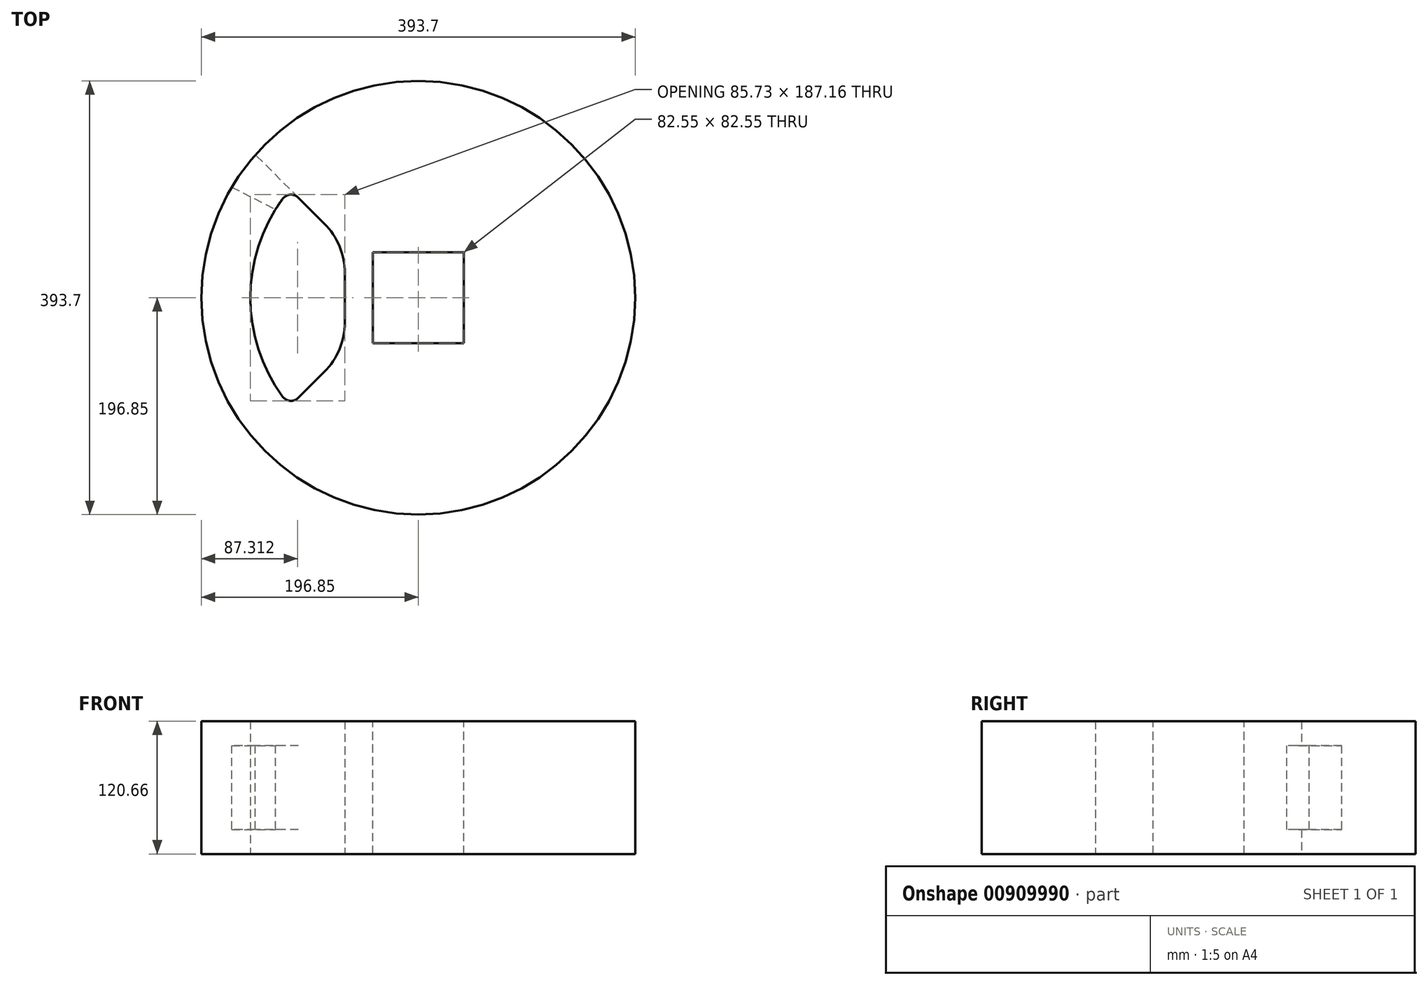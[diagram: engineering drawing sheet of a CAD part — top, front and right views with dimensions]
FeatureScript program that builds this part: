
annotation { "Feature Type Name" : "Feature", "Feature Type Description" : "" }
export const myFeature = defineFeature(function(context is Context, id is Id, definition is map)
    precondition{}
    {
        {
            var Q0;
            Q0=qCreatedBy(makeId("Front.planeOp"),FACE);
            var sketch = newSketch(context, id + "F0", { "sketchPlane" : qUnion([Q0])});
            skLineSegment(sketch, "E0.bottom", {"start": v(0, -60.33) * mm, "end": v(196.85, -60.33) * mm});
            skLineSegment(sketch, "E0.top", {"start": v(0, 60.33) * mm, "end": v(196.85, 60.33) * mm});
            skLineSegment(sketch, "E0.left", {"start": v(0, -60.33) * mm, "end": v(0, 60.32) * mm});
            skLineSegment(sketch, "E0.right", {"start": v(196.85, -60.33) * mm, "end": v(196.85, 60.33) * mm});
            skLineSegment(sketch, "E1", {"start": v(196.85, 0) * mm, "end": v(0, 0) * mm, "construction": true});
            skLineSegment(sketch, "E2", {"start": v(0, 60.33) * mm, "end": v(0, 111.18) * mm, "construction": true});
            skSolve(sketch);
        }
        {
            var Q0;
            Q0=makeQuery(id+"F0.imprint","IMPRINT",FACE,{"disambiguationData":[TD([[makeQuery(id+"F0.imprint","IMPRINT",EDGE,{"derivedFrom":sQuery(id+"F0.wireOp",EDGE,"E0.bottom")}),1.0]])]});
            var Q1;
            Q1=sQuery(id+"F0.wireOp",EDGE,"E0.left");
            revolve(context, id + "F1", {"surfaceOperationType" : NewSurfaceOperationType.NEW, "entities" : qUnion([Q0]), "axis" : qUnion([Q1]), "revolveType" : RevolveType.FULL});
        }
        {
            var Q0;
            Q0=qCreatedBy(makeId("Top.planeOp"),FACE);
            var sketch = newSketch(context, id + "F2", { "sketchPlane" : qUnion([Q0])});
            skArc(sketch, "E3", {"start": v(-116.37, 98.4) * mm, "mid": v(-152.4, 0) * mm, "end": v(-116.37, -98.4) * mm});
            skLineSegment(sketch, "E4.left", {"start": v(-66.67, 22.41) * mm, "end": v(-66.67, -22.41) * mm});
            skLineSegment(sketch, "E5", {"start": v(-116.37, -98.4) * mm, "end": v(-85.27, -67.31) * mm});
            skLineSegment(sketch, "E6", {"start": v(-116.37, 98.4) * mm, "end": v(-85.27, 67.31) * mm});
            skLineSegment(sketch, "E7.bottom", {"start": v(-41.28, 41.28) * mm, "end": v(41.28, 41.28) * mm});
            skLineSegment(sketch, "E7.top", {"start": v(-41.27, -41.28) * mm, "end": v(41.28, -41.28) * mm});
            skLineSegment(sketch, "E7.left", {"start": v(-41.28, 41.28) * mm, "end": v(-41.28, -41.28) * mm});
            skLineSegment(sketch, "E7.right", {"start": v(41.28, 41.28) * mm, "end": v(41.27, -41.28) * mm});
            skLineSegment(sketch, "E8", {"start": v(0, 41.28) * mm, "end": v(0, -41.28) * mm, "construction": true});
            skLineSegment(sketch, "E9", {"start": v(41.28, 0) * mm, "end": v(-41.28, 0) * mm, "construction": true});
            skPoint(sketch, "E10.visualSharp", {"position": v(-66.68, 48.71) * mm});
            skArc(sketch, "E10.filletArc", {"start": v(-66.67, 22.41) * mm, "mid": v(-71.5, 46.71) * mm, "end": v(-85.27, 67.31) * mm});
            skPoint(sketch, "E11.visualSharp", {"position": v(-66.67, -48.71) * mm});
            skArc(sketch, "E11.filletArc", {"start": v(-85.27, -67.31) * mm, "mid": v(-71.5, -46.71) * mm, "end": v(-66.67, -22.41) * mm});
            skLineSegment(sketch, "E12", {"start": v(-116.37, 98.4) * mm, "end": v(-147.88, 129.92) * mm});
            skLineSegment(sketch, "E13", {"start": v(-169.26, 100.5) * mm, "end": v(-129.55, 80.26) * mm});
            skArc(sketch, "E14", {"start": v(-147.88, 129.92) * mm, "mid": v(-159.25, 115.7) * mm, "end": v(-169.26, 100.5) * mm});
            skSolve(sketch);
        }
        {
            var Q0;
            Q0=makeQuery(id+"F2.imprint","IMPRINT",FACE,{"disambiguationData":[TD([[makeQuery(id+"F2.imprint","IMPRINT",EDGE,{"derivedFrom":sQuery(id+"F2.wireOp",EDGE,"E3")}),1.0]])]});
            extrude(context, id + "F3", {"entities" : qUnion([Q0]), "operationType" : NewBodyOperationType.REMOVE, "depth" : 254 * mm, "offsetDistance" : 25 * mm, "symmetric" : true});
        }
        {
            var Q0;
            Q0=makeQuery(id+"F2.imprint","IMPRINT",FACE,{"disambiguationData":[TD([[makeQuery(id+"F2.imprint","IMPRINT",EDGE,{"derivedFrom":sQuery(id+"F2.wireOp",EDGE,"E7.bottom")}),-1.0]])]});
            extrude(context, id + "F4", {"entities" : qUnion([Q0]), "operationType" : NewBodyOperationType.REMOVE, "oppositeDirection" : true, "depth" : 254 * mm, "offsetDistance" : 25 * mm, "symmetric" : true});
        }
        {
            var Q0;
            {var subQ3=sQuery(id+"F2.wireOp",EDGE,"E13");Q0=makeQuery(id+"F2.imprint","IMPRINT",FACE,{"disambiguationData":[TD([[makeQuery(id+"F2.imprint","IMPRINT",EDGE,{"derivedFrom":subQ3}),1.0]])]});}
            extrude(context, id + "F5", {"entities" : qUnion([Q0]), "operationType" : NewBodyOperationType.REMOVE, "oppositeDirection" : true, "depth" : 76.2 * mm, "offsetDistance" : 25 * mm, "symmetric" : true});
        }
        {
            var Q0;
            {var subQ0=sQuery(id+"F2.wireOp",EDGE,"E12");var subQ1=sQuery(id+"F2.wireOp",EDGE,"E3");var subQ2=sQuery(id+"F2.wireOp",EDGE,"E6");Q0=makeQuery(id+"Ftkbro10xyOsZEL_1.15.F5.boolean.opBoolean","SPLIT",EDGE,{"disambiguationData":[TD([makeQuery(id+"F1.opRevolve","SWEPT_FACE",FACE,{"disambiguationData":[OSD([sQuery(id+"F0.wireOp",EDGE,"E0.top")])]})])],"derivedFrom":makeQuery(id+"F5JEKc9ybANWdKY_1.3.F3.boolean.opBoolean","COPY",EDGE,{"derivedFrom":makeQuery(id+"F5JEKc9ybANWdKY_1.3.F3.opExtrude","SWEPT_EDGE",EDGE,{"disambiguationData":[OSD([subQ1,subQ2,subQ0])]})})});}
            var Q1;
            {var subQ0=sQuery(id+"F2.wireOp",EDGE,"E6");var subQ1=sQuery(id+"F2.wireOp",EDGE,"E12");var subQ2=sQuery(id+"F2.wireOp",EDGE,"E3");Q1=makeQuery(id+"Ftkbro10xyOsZEL_1.15.F5.boolean.opBoolean","SPLIT",EDGE,{"disambiguationData":[TD([makeQuery(id+"F1.opRevolve","SWEPT_FACE",FACE,{"disambiguationData":[OSD([sQuery(id+"F0.wireOp",EDGE,"E0.bottom")])]})])],"derivedFrom":makeQuery(id+"F5JEKc9ybANWdKY_1.3.F3.boolean.opBoolean","COPY",EDGE,{"derivedFrom":makeQuery(id+"F5JEKc9ybANWdKY_1.3.F3.opExtrude","SWEPT_EDGE",EDGE,{"disambiguationData":[OSD([subQ2,subQ0,subQ1])]})})});}
            var Q2;
            {var subQ0=sQuery(id+"F2.wireOp",EDGE,"E3");var subQ2=sQuery(id+"F2.wireOp",EDGE,"E5");Q2=makeQuery(id+"Ftkbro10xyOsZEL_1.16.F5.boolean.opBoolean","SPLIT",EDGE,{"disambiguationData":[TD([makeQuery(id+"F1.opRevolve","SWEPT_FACE",FACE,{"disambiguationData":[OSD([sQuery(id+"F0.wireOp",EDGE,"E0.top")])]})])],"derivedFrom":makeQuery(id+"F3.boolean.opBoolean","COPY",EDGE,{"derivedFrom":makeQuery(id+"F3.opExtrude","SWEPT_EDGE",EDGE,{"disambiguationData":[OSD([subQ0,subQ2])]})})});}
            var Q3;
            {var subQ1=sQuery(id+"F2.wireOp",EDGE,"E3");var subQ2=sQuery(id+"F2.wireOp",EDGE,"E5");Q3=makeQuery(id+"Ftkbro10xyOsZEL_1.16.F5.boolean.opBoolean","SPLIT",EDGE,{"disambiguationData":[TD([makeQuery(id+"F1.opRevolve","SWEPT_FACE",FACE,{"disambiguationData":[OSD([sQuery(id+"F0.wireOp",EDGE,"E0.bottom")])]})])],"derivedFrom":makeQuery(id+"F3.boolean.opBoolean","COPY",EDGE,{"derivedFrom":makeQuery(id+"F3.opExtrude","SWEPT_EDGE",EDGE,{"disambiguationData":[OSD([subQ1,subQ2])]})})});}
            var Q4;
            {var subQ0=sQuery(id+"F2.wireOp",EDGE,"E12");var subQ1=sQuery(id+"F2.wireOp",EDGE,"E3");var subQ2=sQuery(id+"F2.wireOp",EDGE,"E6");Q4=makeQuery(id+"Ftkbro10xyOsZEL_1.10.F5.boolean.opBoolean","SPLIT",EDGE,{"disambiguationData":[TD([makeQuery(id+"F1.opRevolve","SWEPT_FACE",FACE,{"disambiguationData":[OSD([sQuery(id+"F0.wireOp",EDGE,"E0.top")])]})])],"derivedFrom":makeQuery(id+"F5JEKc9ybANWdKY_1.2.F3.boolean.opBoolean","COPY",EDGE,{"derivedFrom":makeQuery(id+"F5JEKc9ybANWdKY_1.2.F3.opExtrude","SWEPT_EDGE",EDGE,{"disambiguationData":[OSD([subQ1,subQ2,subQ0])]})})});}
            var Q5;
            {var subQ0=sQuery(id+"F2.wireOp",EDGE,"E6");var subQ1=sQuery(id+"F2.wireOp",EDGE,"E12");var subQ2=sQuery(id+"F2.wireOp",EDGE,"E3");Q5=makeQuery(id+"Ftkbro10xyOsZEL_1.10.F5.boolean.opBoolean","SPLIT",EDGE,{"disambiguationData":[TD([makeQuery(id+"F1.opRevolve","SWEPT_FACE",FACE,{"disambiguationData":[OSD([sQuery(id+"F0.wireOp",EDGE,"E0.bottom")])]})])],"derivedFrom":makeQuery(id+"F5JEKc9ybANWdKY_1.2.F3.boolean.opBoolean","COPY",EDGE,{"derivedFrom":makeQuery(id+"F5JEKc9ybANWdKY_1.2.F3.opExtrude","SWEPT_EDGE",EDGE,{"disambiguationData":[OSD([subQ2,subQ0,subQ1])]})})});}
            var Q6;
            {var subQ0=sQuery(id+"F2.wireOp",EDGE,"E5");var subQ2=sQuery(id+"F2.wireOp",EDGE,"E3");Q6=makeQuery(id+"Ftkbro10xyOsZEL_1.11.F5.boolean.opBoolean","SPLIT",EDGE,{"disambiguationData":[TD([makeQuery(id+"F1.opRevolve","SWEPT_FACE",FACE,{"disambiguationData":[OSD([sQuery(id+"F0.wireOp",EDGE,"E0.top")])]})])],"derivedFrom":makeQuery(id+"F5JEKc9ybANWdKY_1.3.F3.boolean.opBoolean","COPY",EDGE,{"derivedFrom":makeQuery(id+"F5JEKc9ybANWdKY_1.3.F3.opExtrude","SWEPT_EDGE",EDGE,{"disambiguationData":[OSD([subQ2,subQ0])]})})});}
            var Q7;
            {var subQ1=sQuery(id+"F2.wireOp",EDGE,"E3");var subQ2=sQuery(id+"F2.wireOp",EDGE,"E5");Q7=makeQuery(id+"Ftkbro10xyOsZEL_1.11.F5.boolean.opBoolean","SPLIT",EDGE,{"disambiguationData":[TD([makeQuery(id+"F1.opRevolve","SWEPT_FACE",FACE,{"disambiguationData":[OSD([sQuery(id+"F0.wireOp",EDGE,"E0.bottom")])]})])],"derivedFrom":makeQuery(id+"F5JEKc9ybANWdKY_1.3.F3.boolean.opBoolean","COPY",EDGE,{"derivedFrom":makeQuery(id+"F5JEKc9ybANWdKY_1.3.F3.opExtrude","SWEPT_EDGE",EDGE,{"disambiguationData":[OSD([subQ1,subQ2])]})})});}
            var Q8;
            {var subQ0=sQuery(id+"F2.wireOp",EDGE,"E12");var subQ1=sQuery(id+"F2.wireOp",EDGE,"E3");var subQ2=sQuery(id+"F2.wireOp",EDGE,"E6");Q8=makeQuery(id+"Ftkbro10xyOsZEL_1.5.F5.boolean.opBoolean","SPLIT",EDGE,{"disambiguationData":[TD([makeQuery(id+"F1.opRevolve","SWEPT_FACE",FACE,{"disambiguationData":[OSD([sQuery(id+"F0.wireOp",EDGE,"E0.top")])]})])],"derivedFrom":makeQuery(id+"F5JEKc9ybANWdKY_1.1.F3.boolean.opBoolean","COPY",EDGE,{"derivedFrom":makeQuery(id+"F5JEKc9ybANWdKY_1.1.F3.opExtrude","SWEPT_EDGE",EDGE,{"disambiguationData":[OSD([subQ1,subQ2,subQ0])]})})});}
            var Q9;
            {var subQ0=sQuery(id+"F2.wireOp",EDGE,"E6");var subQ1=sQuery(id+"F2.wireOp",EDGE,"E3");var subQ2=sQuery(id+"F2.wireOp",EDGE,"E12");Q9=makeQuery(id+"Ftkbro10xyOsZEL_1.5.F5.boolean.opBoolean","SPLIT",EDGE,{"disambiguationData":[TD([makeQuery(id+"F1.opRevolve","SWEPT_FACE",FACE,{"disambiguationData":[OSD([sQuery(id+"F0.wireOp",EDGE,"E0.bottom")])]})])],"derivedFrom":makeQuery(id+"F5JEKc9ybANWdKY_1.1.F3.boolean.opBoolean","COPY",EDGE,{"derivedFrom":makeQuery(id+"F5JEKc9ybANWdKY_1.1.F3.opExtrude","SWEPT_EDGE",EDGE,{"disambiguationData":[OSD([subQ1,subQ0,subQ2])]})})});}
            var Q10;
            {var subQ0=sQuery(id+"F2.wireOp",EDGE,"E5");var subQ1=sQuery(id+"F2.wireOp",EDGE,"E3");Q10=makeQuery(id+"Ftkbro10xyOsZEL_1.6.F5.boolean.opBoolean","SPLIT",EDGE,{"disambiguationData":[TD([makeQuery(id+"F1.opRevolve","SWEPT_FACE",FACE,{"disambiguationData":[OSD([sQuery(id+"F0.wireOp",EDGE,"E0.top")])]})])],"derivedFrom":makeQuery(id+"F5JEKc9ybANWdKY_1.2.F3.boolean.opBoolean","COPY",EDGE,{"derivedFrom":makeQuery(id+"F5JEKc9ybANWdKY_1.2.F3.opExtrude","SWEPT_EDGE",EDGE,{"disambiguationData":[OSD([subQ1,subQ0])]})})});}
            var Q11;
            {var subQ1=sQuery(id+"F2.wireOp",EDGE,"E3");var subQ2=sQuery(id+"F2.wireOp",EDGE,"E5");Q11=makeQuery(id+"Ftkbro10xyOsZEL_1.6.F5.boolean.opBoolean","SPLIT",EDGE,{"disambiguationData":[TD([makeQuery(id+"F1.opRevolve","SWEPT_FACE",FACE,{"disambiguationData":[OSD([sQuery(id+"F0.wireOp",EDGE,"E0.bottom")])]})])],"derivedFrom":makeQuery(id+"F5JEKc9ybANWdKY_1.2.F3.boolean.opBoolean","COPY",EDGE,{"derivedFrom":makeQuery(id+"F5JEKc9ybANWdKY_1.2.F3.opExtrude","SWEPT_EDGE",EDGE,{"disambiguationData":[OSD([subQ1,subQ2])]})})});}
            var Q12;
            {var subQ0=sQuery(id+"F2.wireOp",EDGE,"E6");var subQ1=sQuery(id+"F2.wireOp",EDGE,"E12");var subQ2=sQuery(id+"F2.wireOp",EDGE,"E3");Q12=makeQuery(id+"F5.boolean.opBoolean","SPLIT",EDGE,{"disambiguationData":[TD([makeQuery(id+"F1.opRevolve","SWEPT_FACE",FACE,{"disambiguationData":[OSD([sQuery(id+"F0.wireOp",EDGE,"E0.top")])]})])],"derivedFrom":makeQuery(id+"F3.boolean.opBoolean","COPY",EDGE,{"derivedFrom":makeQuery(id+"F3.opExtrude","SWEPT_EDGE",EDGE,{"disambiguationData":[OSD([subQ2,subQ0,subQ1])]})})});}
            var Q13;
            {var subQ0=sQuery(id+"F2.wireOp",EDGE,"E6");var subQ1=sQuery(id+"F2.wireOp",EDGE,"E3");var subQ2=sQuery(id+"F2.wireOp",EDGE,"E12");Q13=makeQuery(id+"F5.boolean.opBoolean","SPLIT",EDGE,{"disambiguationData":[TD([makeQuery(id+"F1.opRevolve","SWEPT_FACE",FACE,{"disambiguationData":[OSD([sQuery(id+"F0.wireOp",EDGE,"E0.bottom")])]})])],"derivedFrom":makeQuery(id+"F3.boolean.opBoolean","COPY",EDGE,{"derivedFrom":makeQuery(id+"F3.opExtrude","SWEPT_EDGE",EDGE,{"disambiguationData":[OSD([subQ1,subQ0,subQ2])]})})});}
            var Q14;
            {var subQ0=sQuery(id+"F2.wireOp",EDGE,"E5");var subQ2=sQuery(id+"F2.wireOp",EDGE,"E3");Q14=makeQuery(id+"Ftkbro10xyOsZEL_1.1.F5.boolean.opBoolean","SPLIT",EDGE,{"disambiguationData":[TD([makeQuery(id+"F1.opRevolve","SWEPT_FACE",FACE,{"disambiguationData":[OSD([sQuery(id+"F0.wireOp",EDGE,"E0.top")])]})])],"derivedFrom":makeQuery(id+"F5JEKc9ybANWdKY_1.1.F3.boolean.opBoolean","COPY",EDGE,{"derivedFrom":makeQuery(id+"F5JEKc9ybANWdKY_1.1.F3.opExtrude","SWEPT_EDGE",EDGE,{"disambiguationData":[OSD([subQ2,subQ0])]})})});}
            var Q15;
            {var subQ1=sQuery(id+"F2.wireOp",EDGE,"E3");var subQ2=sQuery(id+"F2.wireOp",EDGE,"E5");Q15=makeQuery(id+"Ftkbro10xyOsZEL_1.1.F5.boolean.opBoolean","SPLIT",EDGE,{"disambiguationData":[TD([makeQuery(id+"F1.opRevolve","SWEPT_FACE",FACE,{"disambiguationData":[OSD([sQuery(id+"F0.wireOp",EDGE,"E0.bottom")])]})])],"derivedFrom":makeQuery(id+"F5JEKc9ybANWdKY_1.1.F3.boolean.opBoolean","COPY",EDGE,{"derivedFrom":makeQuery(id+"F5JEKc9ybANWdKY_1.1.F3.opExtrude","SWEPT_EDGE",EDGE,{"disambiguationData":[OSD([subQ1,subQ2])]})})});}
            fillet(context, id + "F6", {"entities" : qUnion([Q0, Q1, Q2, Q3, Q4, Q5, Q6, Q7, Q8, Q9, Q10, Q11, Q12, Q13, Q14, Q15]), "radius" : 9.53 * mm, "tangentPropagation" : true, "allowEdgeOverflow" : false});
        }
    });
